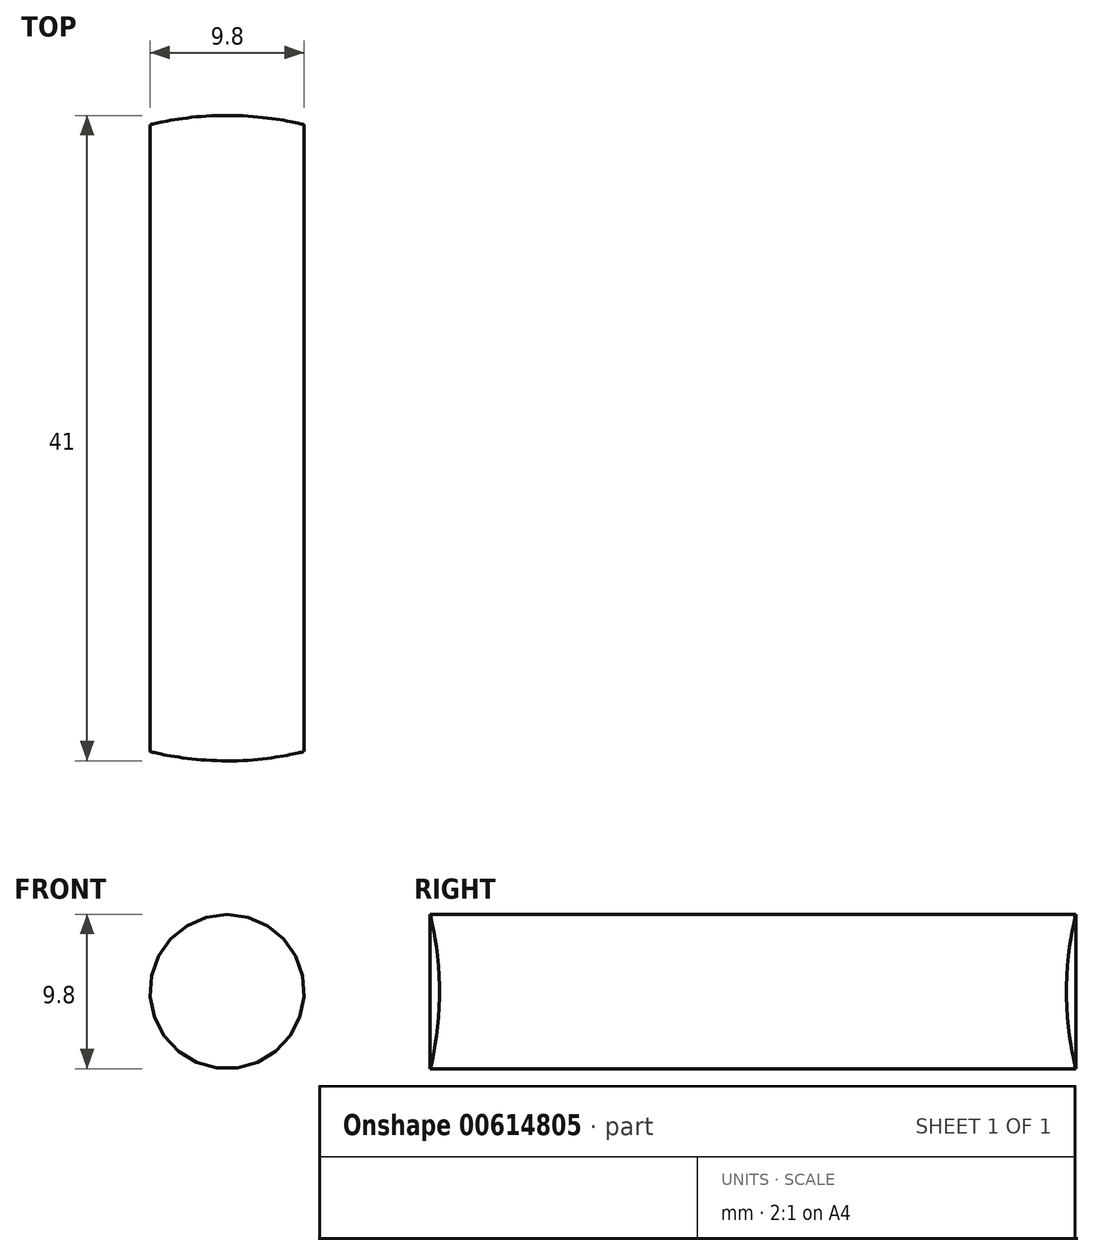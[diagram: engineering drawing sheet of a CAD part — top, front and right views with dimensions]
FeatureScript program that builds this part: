
annotation { "Feature Type Name" : "Feature", "Feature Type Description" : "" }
export const myFeature = defineFeature(function(context is Context, id is Id, definition is map)
    precondition{}
    {
        {
            var Q0;
            Q0=qCreatedBy(makeId("Front.planeOp"),FACE);
            var sketch = newSketch(context, id + "F0", { "sketchPlane" : qUnion([Q0])});
            skCircle(sketch, "E0", {"center": v(0, 0) * mm, "radius": 4.9 * mm});
            skSolve(sketch);
        }
        {
            var Q0;
            Q0 = qSketchRegion(id + "F0", true);
            extrude(context, id + "F1", {"entities" : qUnion([Q0]), "depth" : 20.5 * mm, "offsetDistance" : 25 * mm, "hasSecondDirection" : true, "secondDirectionOppositeDirection" : true, "secondDirectionDepth" : 20.5 * mm});
        }
        {
            var Q0;
            Q0=qCreatedBy(makeId("Top.planeOp"),FACE);
            var sketch = newSketch(context, id + "F2", { "sketchPlane" : qUnion([Q0])});
            skCircle(sketch, "E1", {"center": v(0, 0) * mm, "radius": 20.5 * mm});
            skLineSegment(sketch, "E2.0.0", {"start": v(4.9, -20.5) * mm, "end": v(-4.9, -20.5) * mm});
            skLineSegment(sketch, "E3.0", {"start": v(4.9, 20.5) * mm, "end": v(-4.9, 20.5) * mm});
            skSolve(sketch);
        }
        {
            var Q0;
            Q0=makeQuery(id+"F2.imprint","IMPRINT",FACE,{"disambiguationData":[TD([[makeQuery(id+"F2.imprint","IMPRINT",EDGE,{"derivedFrom":sQuery(id+"F2.wireOp",EDGE,"E1")}),1.0]])]});
            extrude(context, id + "F3", {"entities" : qUnion([Q0]), "operationType" : NewBodyOperationType.INTERSECT, "oppositeDirection" : true, "depth" : 25 * mm, "offsetDistance" : 25 * mm, "hasSecondDirection" : true, "secondDirectionOppositeDirection" : false, "secondDirectionDepth" : 25 * mm});
        }
    });
